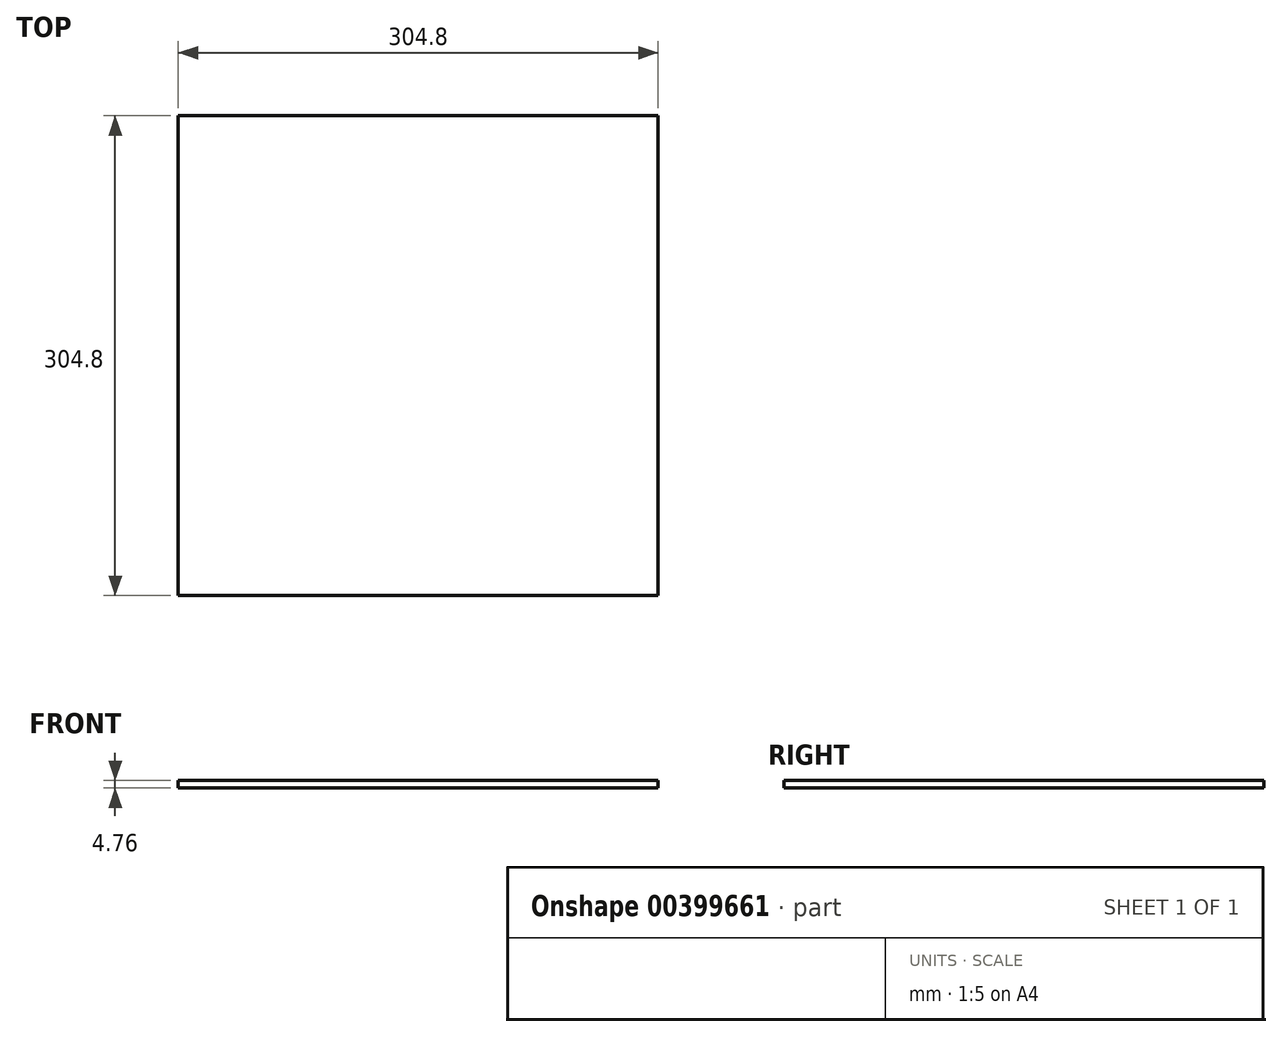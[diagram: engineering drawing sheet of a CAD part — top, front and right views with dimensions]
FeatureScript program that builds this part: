
annotation { "Feature Type Name" : "Feature", "Feature Type Description" : "" }
export const myFeature = defineFeature(function(context is Context, id is Id, definition is map)
    precondition{}
    {
        {
            var Q0;
            Q0=qCreatedBy(makeId("Top.planeOp"),FACE);
            var sketch = newSketch(context, id + "F0", { "sketchPlane" : qUnion([Q0])});
            skLineSegment(sketch, "E0.bottom", {"start": v(0, 0) * mm, "end": v(304.8, 0) * mm});
            skLineSegment(sketch, "E0.top", {"start": v(0, 304.8) * mm, "end": v(304.8, 304.8) * mm});
            skLineSegment(sketch, "E0.left", {"start": v(0, 0) * mm, "end": v(0, 304.8) * mm});
            skLineSegment(sketch, "E0.right", {"start": v(304.8, 0) * mm, "end": v(304.8, 304.8) * mm});
            skSolve(sketch);
        }
        {
            var Q0;
            Q0 = qSketchRegion(id + "F0", true);
            extrude(context, id + "F1", {"entities" : qUnion([Q0]), "depth" : 4.76 * mm});
        }
    });
